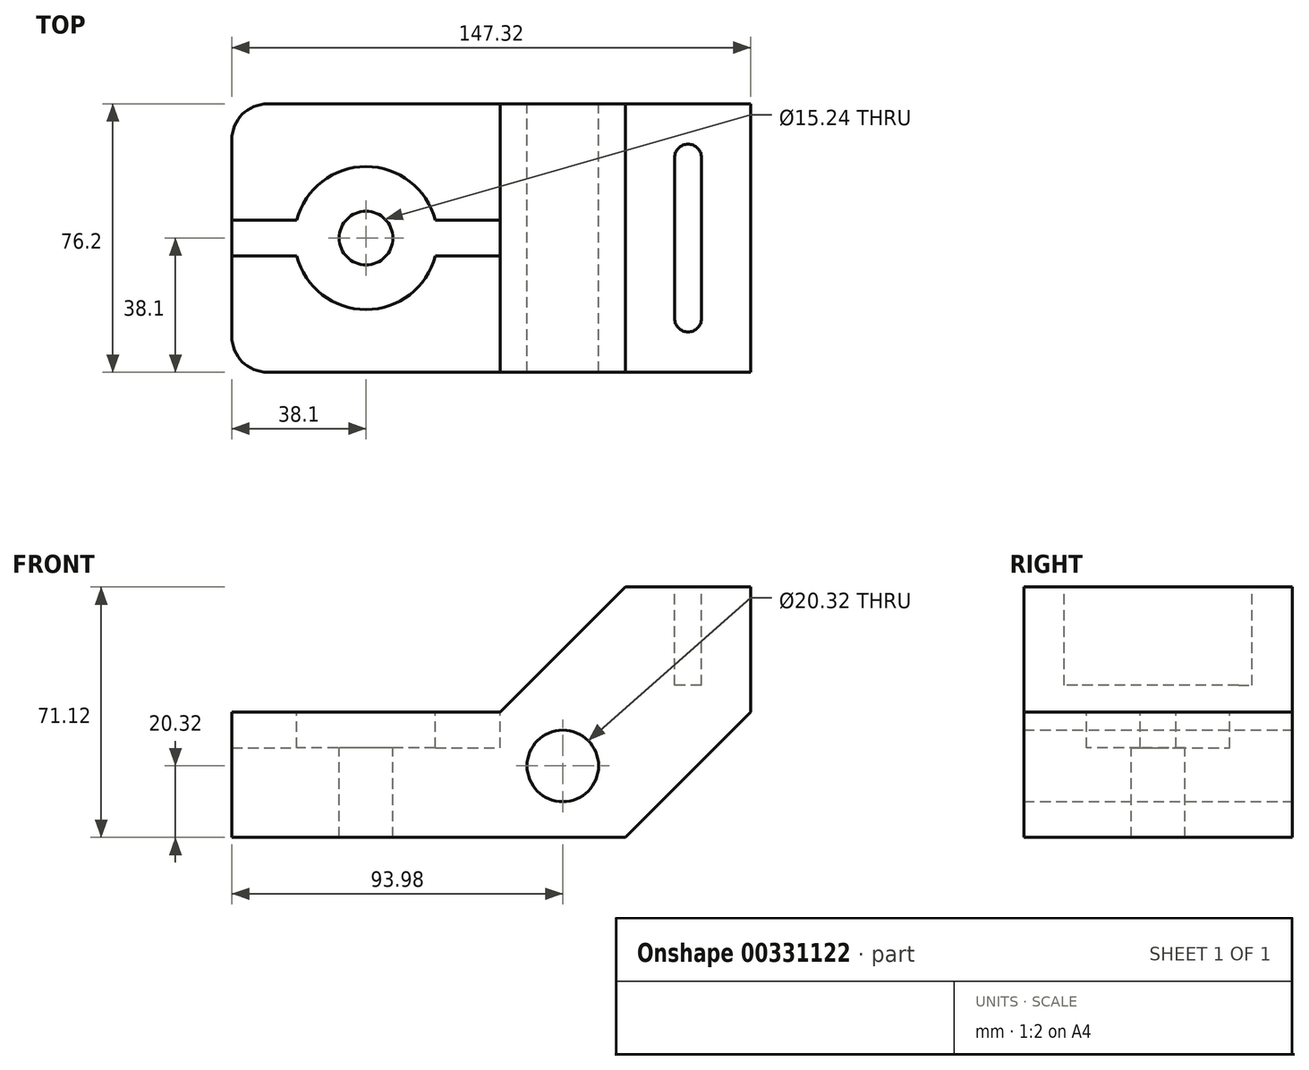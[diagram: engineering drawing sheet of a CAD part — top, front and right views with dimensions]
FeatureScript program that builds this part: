
annotation { "Feature Type Name" : "Feature", "Feature Type Description" : "" }
export const myFeature = defineFeature(function(context is Context, id is Id, definition is map)
    precondition{}
    {
        {
            var Q0;
            Q0=qCreatedBy(makeId("Front.planeOp"),FACE);
            var sketch = newSketch(context, id + "F0", { "sketchPlane" : qUnion([Q0])});
            skLineSegment(sketch, "E0", {"start": v(0, 0) * mm, "end": v(0, 35.56) * mm});
            skLineSegment(sketch, "E1", {"start": v(0, 35.56) * mm, "end": v(76.2, 35.56) * mm});
            skLineSegment(sketch, "E2", {"start": v(76.2, 35.56) * mm, "end": v(111.76, 71.12) * mm});
            skLineSegment(sketch, "E3", {"start": v(111.76, 71.12) * mm, "end": v(147.32, 71.12) * mm});
            skLineSegment(sketch, "E4", {"start": v(147.32, 71.12) * mm, "end": v(147.32, 35.56) * mm});
            skLineSegment(sketch, "E5", {"start": v(147.32, 35.56) * mm, "end": v(111.76, 0) * mm});
            skLineSegment(sketch, "E6", {"start": v(111.76, 0) * mm, "end": v(0, 0) * mm});
            skCircle(sketch, "E7", {"center": v(93.98, 20.32) * mm, "radius": 10.16 * mm});
            skSolve(sketch);
        }
        {
            var Q0;
            Q0 = qSketchRegion(id + "F0", true);
            extrude(context, id + "F1", {"entities" : qUnion([Q0]), "depth" : 76.2 * mm});
        }
        {
            var Q0;
            Q0=makeQuery(id+"F1.opExtrude","SWEPT_FACE",FACE,{"disambiguationData":[OSD([sQuery(id+"F0.wireOp",EDGE,"E3")])]});
            var sketch = newSketch(context, id + "F2", { "sketchPlane" : qUnion([Q0])});
            skArc(sketch, "E8", {"start": v(133.35, -15.24) * mm, "mid": v(129.54, -11.43) * mm, "end": v(125.73, -15.24) * mm});
            skArc(sketch, "E9", {"start": v(125.73, -60.96) * mm, "mid": v(129.54, -64.77) * mm, "end": v(133.35, -60.96) * mm});
            skLineSegment(sketch, "E10", {"start": v(125.73, -15.24) * mm, "end": v(125.73, -60.96) * mm});
            skLineSegment(sketch, "E11", {"start": v(133.35, -15.24) * mm, "end": v(133.35, -60.96) * mm});
            skSolve(sketch);
        }
        {
            var Q0;
            Q0 = qSketchRegion(id + "F2", true);
            extrude(context, id + "F3", {"entities" : qUnion([Q0]), "operationType" : NewBodyOperationType.REMOVE, "oppositeDirection" : true, "depth" : 27.94 * mm});
        }
        {
            var Q0;
            Q0=makeQuery(id+"F1.opExtrude","SWEPT_FACE",FACE,{"disambiguationData":[OSD([sQuery(id+"F0.wireOp",EDGE,"E1")])]});
            var sketch = newSketch(context, id + "F4", { "sketchPlane" : qUnion([Q0])});
            skLineSegment(sketch, "E12", {"start": v(0, -33.02) * mm, "end": v(76.2, -33.02) * mm});
            skPoint(sketch, "E13", {"position": v(38.1, -38.1) * mm});
            skLineSegment(sketch, "E14", {"start": v(0, -43.18) * mm, "end": v(76.2, -43.18) * mm});
            skLineSegment(sketch, "E15", {"start": v(76.2, -43.18) * mm, "end": v(76.2, -33.02) * mm});
            skLineSegment(sketch, "E16", {"start": v(0, -33.02) * mm, "end": v(0, -43.18) * mm});
            skSolve(sketch);
        }
        {
            var Q0;
            Q0 = qSketchRegion(id + "F4", true);
            extrude(context, id + "F5", {"entities" : qUnion([Q0]), "operationType" : NewBodyOperationType.REMOVE, "oppositeDirection" : true, "depth" : 10.16 * mm});
        }
        {
            var Q0;
            Q0=sQuery(id+"F4.wireOp",VERTEX,"E13");
            var Q1;
            Q1=makeQuery(id+"F1.opExtrude","SWEPT_BODY",BODY,{"disambiguationData":[OSD([sQuery(id+"F0.wireOp",EDGE,"E0"),sQuery(id+"F0.wireOp",EDGE,"E1"),sQuery(id+"F0.wireOp",EDGE,"E2"),sQuery(id+"F0.wireOp",EDGE,"E3"),sQuery(id+"F0.wireOp",EDGE,"E4"),sQuery(id+"F0.wireOp",EDGE,"E5"),sQuery(id+"F0.wireOp",EDGE,"E6"),sQuery(id+"F0.wireOp",EDGE,"E7")])]});
            hole(context, id + "F6", {"style" : HoleStyle.C_BORE, "endStyle" : HoleEndStyle.THROUGH, "holeDiameter" : 15.24 * mm, "cBoreDiameter" : 40.64 * mm, "cBoreDepth" : 0 * mm, "tappedDepth" : 12.7 * mm, "tapClearance" : 3, "locations" : qUnion([Q0]), "scope" : qUnion([Q1])});
        }
        {
            var Q0;
            Q0=makeQuery(id+"F1.opExtrude","CAP_EDGE",EDGE,{"disambiguationData":[OSD([sQuery(id+"F0.wireOp",EDGE,"E0")])],"isStart":true});
            var Q1;
            Q1=makeQuery(id+"F1.opExtrude","CAP_EDGE",EDGE,{"disambiguationData":[OSD([sQuery(id+"F0.wireOp",EDGE,"E0")])],"isStart":false});
            fillet(context, id + "F7", {"entities" : qUnion([Q0, Q1]), "radius" : 10.16 * mm, "tangentPropagation" : true, "allowEdgeOverflow" : false});
        }
    });
